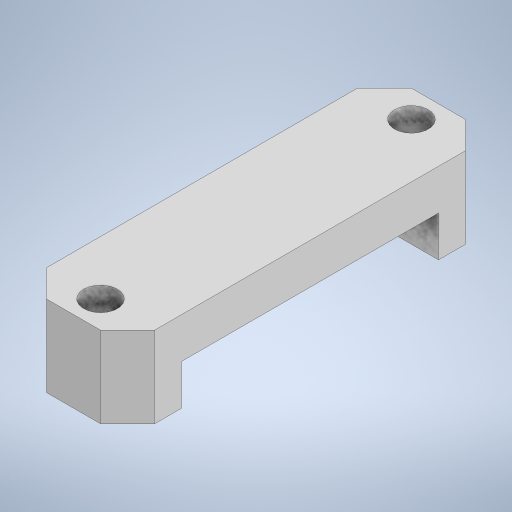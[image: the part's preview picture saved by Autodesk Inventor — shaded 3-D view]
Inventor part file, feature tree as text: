
AUTODESK INVENTOR PART (.ipt)
format: ipt  version: 2023 (Build 270158000, 158)  size: 232,448 bytes
history: native  units: mm
features: extrude x2, other x1, sketch x1, chamfer x1
ambient origin geometry x8: Origin, YZ Plane, XZ Plane, XY Plane, X Axis, Y Axis, Z Axis, Center Point
bodies: Body1 (feature_tree)
feature tree (5):
  other  "솔리드1"
  sketch  "스케치1"
  extrude  "돌출1"  Depth=8.0mm
  extrude  "돌출2"  Depth=27.0mm
  chamfer  "모따기1"  Distance=4.0mm
